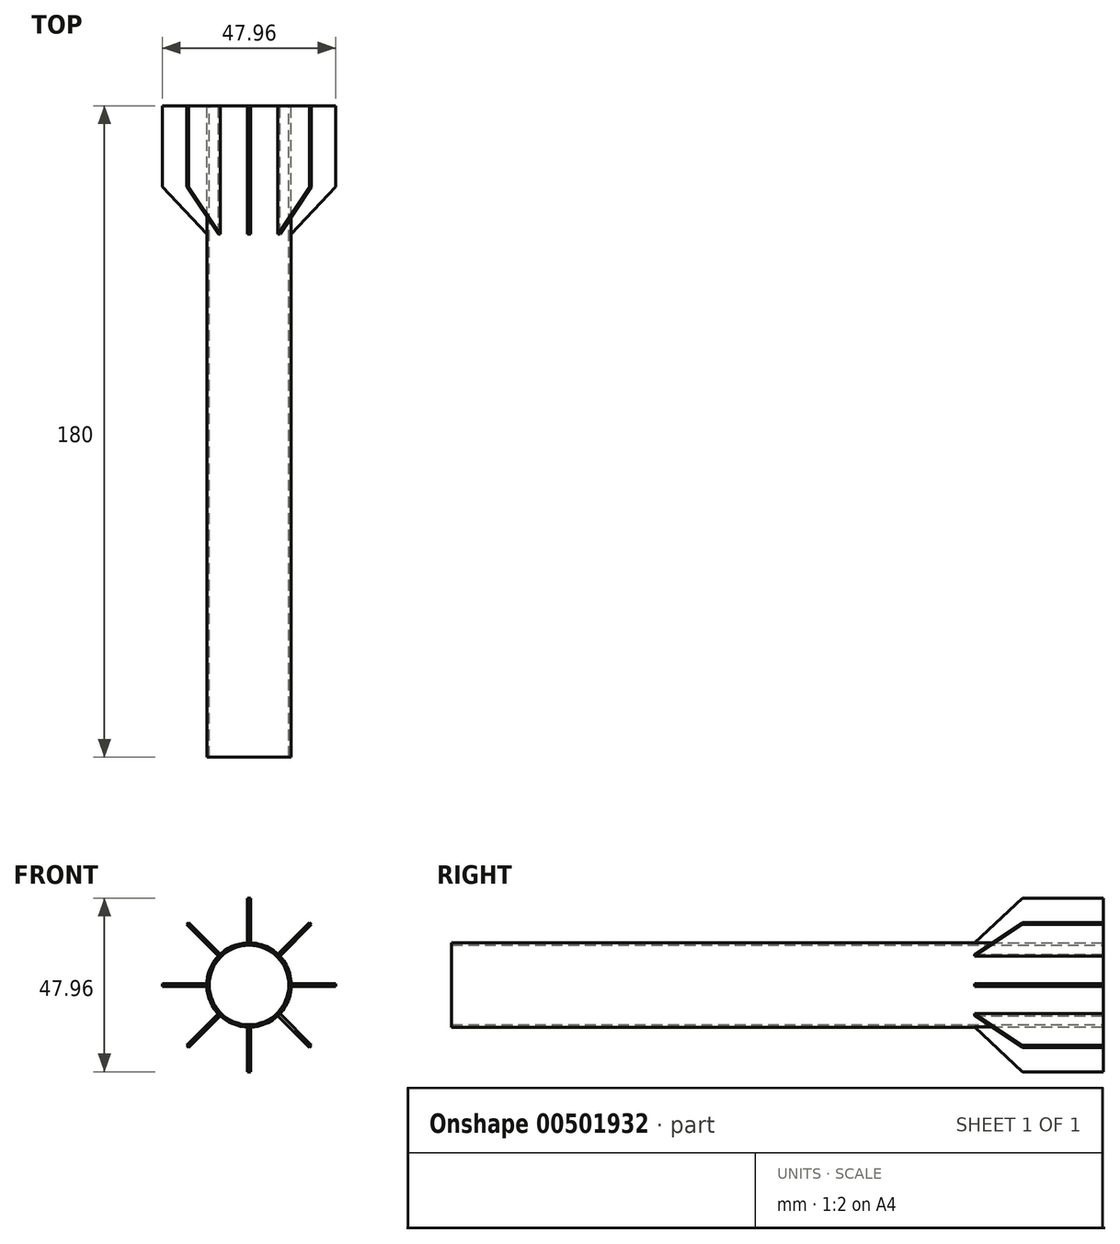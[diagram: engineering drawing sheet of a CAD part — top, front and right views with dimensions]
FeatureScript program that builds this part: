
annotation { "Feature Type Name" : "Feature", "Feature Type Description" : "" }
export const myFeature = defineFeature(function(context is Context, id is Id, definition is map)
    precondition{}
    {
        {
            var Q0;
            Q0=qCreatedBy(makeId("Front.planeOp"),FACE);
            var sketch = newSketch(context, id + "F0", { "sketchPlane" : qUnion([Q0])});
            skCircle(sketch, "E0", {"center": v(0, 0) * mm, "radius": 11 * mm});
            skCircle(sketch, "E1", {"center": v(0, 0) * mm, "radius": 11.65 * mm});
            skSolve(sketch);
        }
        {
            var Q0;
            Q0=makeQuery(id+"F0.imprint","IMPRINT",FACE,{"disambiguationData":[TD([[makeQuery(id+"F0.imprint","IMPRINT",EDGE,{"derivedFrom":sQuery(id+"F0.wireOp",EDGE,"E0")}),-1.0]])]});
            extrude(context, id + "F1", {"entities" : qUnion([Q0]), "depth" : 180 * mm});
        }
        {
            var Q0;
            Q0=qCreatedBy(makeId("Top.planeOp"),FACE);
            var sketch = newSketch(context, id + "F2", { "sketchPlane" : qUnion([Q0])});
            skLineSegment(sketch, "E2", {"start": v(-11.32, 0) * mm, "end": v(-11.32, -35.87) * mm});
            skLineSegment(sketch, "E3", {"start": v(-11.32, -35.87) * mm, "end": v(-23.98, -22.38) * mm});
            skLineSegment(sketch, "E4", {"start": v(-23.98, -22.38) * mm, "end": v(-23.98, 0) * mm});
            skLineSegment(sketch, "E5", {"start": v(-23.98, 0) * mm, "end": v(-11.32, 0) * mm});
            skSolve(sketch);
        }
        {
            var Q0;
            Q0=makeQuery(id+"F2.imprint","IMPRINT",FACE,{"disambiguationData":[TD([[makeQuery(id+"F2.imprint","IMPRINT",EDGE,{"derivedFrom":sQuery(id+"F2.wireOp",EDGE,"E2")}),-1.0]])]});
            extrude(context, id + "F3", {"entities" : qUnion([Q0]), "operationType" : NewBodyOperationType.ADD, "endBound" : BoundingType.SYMMETRIC, "depth" : 0.8 * mm});
        }
        {
            var Q0;
            Q0=makeQuery(id+"F1.opExtrude","SWEPT_BODY",BODY,{"disambiguationData":[OSD([sQuery(id+"F0.wireOp",EDGE,"E0"),sQuery(id+"F0.wireOp",EDGE,"E1")])]});
            var Q1;
            Q1=makeQuery(id+"F1.opExtrude","SWEPT_FACE",FACE,{"disambiguationData":[OSD([sQuery(id+"F0.wireOp",EDGE,"E1")])]});
            circularPattern(context, id + "F4", {"operationType" : NewBodyOperationType.ADD, "entities" : qUnion([Q0]), "axis" : qUnion([Q1]), "angle" : 360 * degree, "instanceCount" : 8, "equalSpace" : true});
        }
    });
